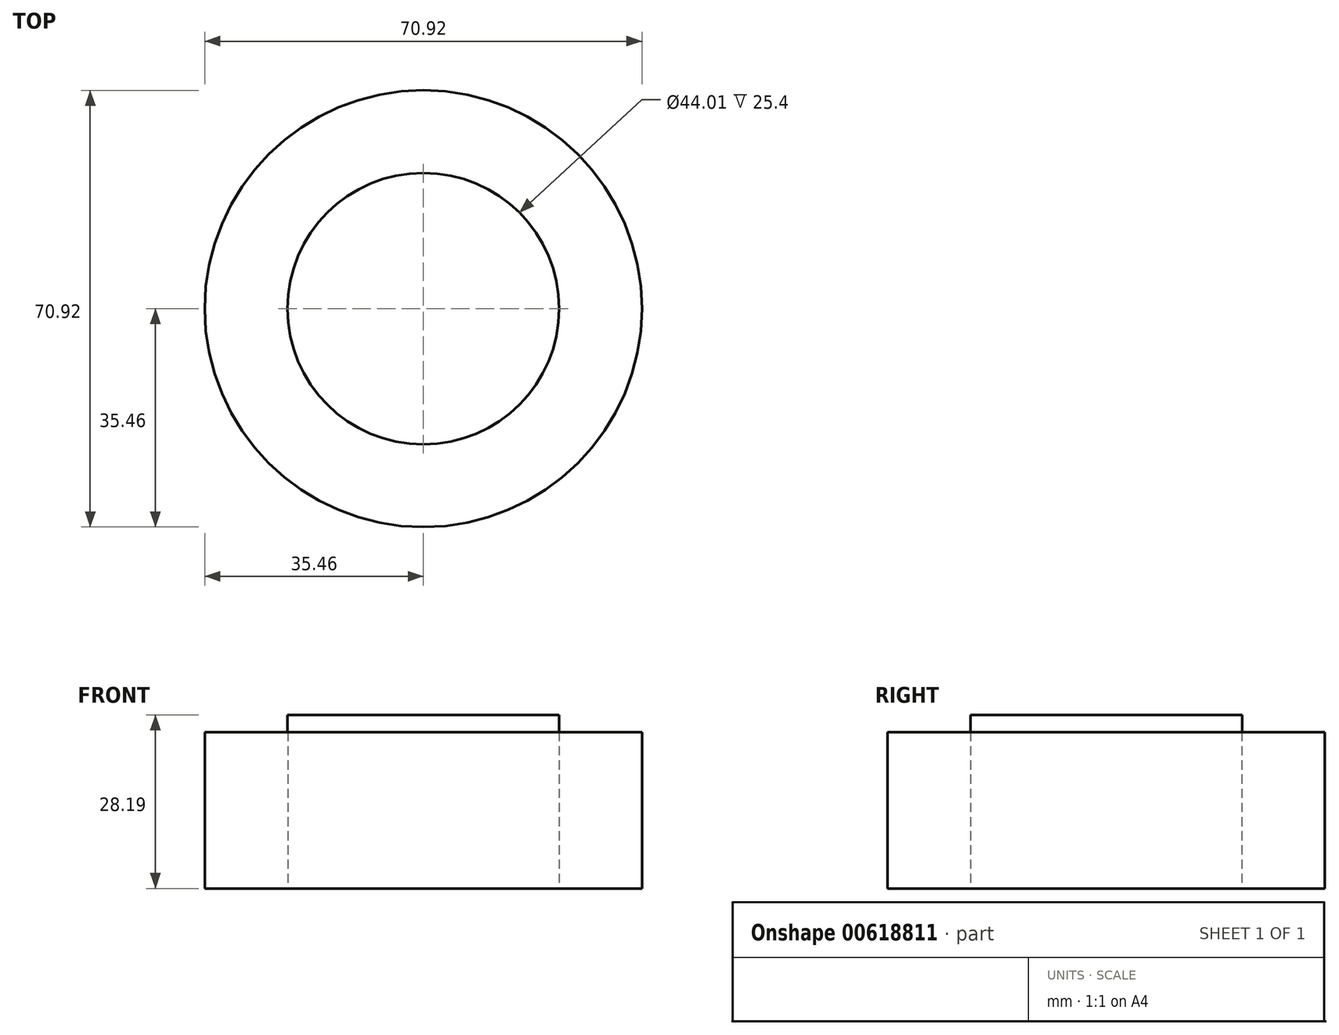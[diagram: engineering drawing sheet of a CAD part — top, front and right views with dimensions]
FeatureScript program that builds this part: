
annotation { "Feature Type Name" : "Feature", "Feature Type Description" : "" }
export const myFeature = defineFeature(function(context is Context, id is Id, definition is map)
    precondition{}
    {
        {
            var Q0;
            Q0=qCreatedBy(makeId("Top.planeOp"),FACE);
            var sketch = newSketch(context, id + "F0", { "sketchPlane" : qUnion([Q0])});
            skCircle(sketch, "E0", {"center": v(0, 0) * mm, "radius": 22 * mm});
            skCircle(sketch, "E1", {"center": v(0, 0) * mm, "radius": 35.46 * mm});
            skSolve(sketch);
        }
        {
            var Q0;
            Q0=qSketchRegion(id+"F0",true);
            extrude(context, id + "F1", {"entities" : qUnion([Q0]), "depth" : 25.4 * mm, "offsetDistance" : 25.4 * mm});
        }
        {
            var Q0;
            Q0=makeQuery(id+"F1.opExtrude","CAP_FACE",FACE,{"disambiguationData":[OSD([sQuery(id+"F0.wireOp",EDGE,"E0"),sQuery(id+"F0.wireOp",EDGE,"E1")])],"isStart":false});
            var sketch = newSketch(context, id + "F2", { "sketchPlane" : qUnion([Q0])});
            skCircle(sketch, "E2", {"center": v(0, 0) * mm, "radius": 22.05 * mm});
            skSolve(sketch);
        }
        {
            var Q0;
            Q0=qSketchRegion(id+"F2",true);
            extrude(context, id + "F3", {"entities" : qUnion([Q0]), "operationType" : NewBodyOperationType.ADD, "depth" : 2.8 * mm, "offsetDistance" : 25.4 * mm});
        }
    });
